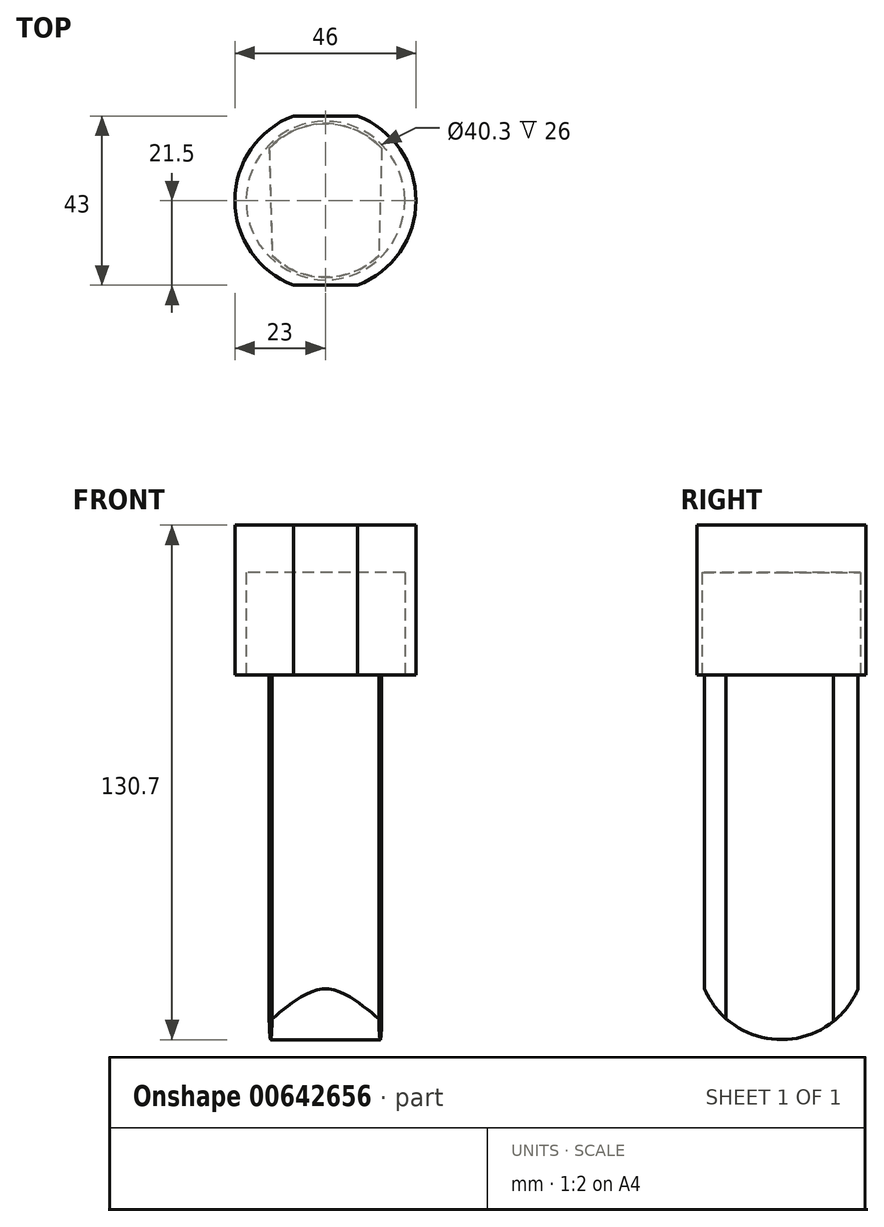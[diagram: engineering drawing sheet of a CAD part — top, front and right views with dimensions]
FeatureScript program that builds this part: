
annotation { "Feature Type Name" : "Feature", "Feature Type Description" : "" }
export const myFeature = defineFeature(function(context is Context, id is Id, definition is map)
    precondition{}
    {
        {
            var Q0;
            Q0=qCreatedBy(makeId("Top.planeOp"),FACE);
            var sketch = newSketch(context, id + "F0", { "sketchPlane" : qUnion([Q0])});
            skArc(sketch, "E0", {"start": v(-8.17, 21.5) * mm, "mid": v(-23, 0) * mm, "end": v(-8.17, -21.5) * mm});
            skLineSegment(sketch, "E1", {"start": v(-8.17, 21.5) * mm, "end": v(8.17, 21.5) * mm});
            skLineSegment(sketch, "E2.MirrorCS", {"start": v(-8.17, -21.5) * mm, "end": v(8.17, -21.5) * mm});
            skArc(sketch, "E3.trimOffspring", {"start": v(8.17, -21.5) * mm, "mid": v(23, 0) * mm, "end": v(8.17, 21.5) * mm});
            skSolve(sketch);
        }
        {
            var Q0;
            Q0 = qSketchRegion(id + "F0", true);
            var Q1;
            Q1=makeQuery(id+"F0.imprint","IMPRINT",FACE,{"disambiguationData":[TD([[makeQuery(id+"F0.imprint","IMPRINT",EDGE,{"derivedFrom":sQuery(id+"F0.wireOp",EDGE,"E0")}),1.0]])]});
            extrude(context, id + "F1", {"entities" : qUnion([Q0, Q1]), "depth" : 38 * mm, "offsetDistance" : 25.4 * mm});
        }
        {
            var Q0;
            Q0=qCreatedBy(makeId("Top.planeOp"),FACE);
            var sketch = newSketch(context, id + "F2", { "sketchPlane" : qUnion([Q0])});
            skCircle(sketch, "E4", {"center": v(0, 0) * mm, "radius": 20.15 * mm});
            skSolve(sketch);
        }
        {
            var Q0;
            Q0=makeQuery(id+"F2.imprint","IMPRINT",FACE,{"disambiguationData":[TD([[makeQuery(id+"F2.imprint","IMPRINT",EDGE,{"derivedFrom":sQuery(id+"F2.wireOp",EDGE,"E4")}),1.0]])]});
            extrude(context, id + "F3", {"entities" : qUnion([Q0]), "operationType" : NewBodyOperationType.REMOVE, "depth" : 26 * mm, "offsetDistance" : 25.4 * mm});
        }
        {
            var Q0;
            Q0=qCreatedBy(makeId("Top.planeOp"),FACE);
            var sketch = newSketch(context, id + "F4", { "sketchPlane" : qUnion([Q0])});
            skArc(sketch, "E5", {"start": v(-13.55, -14.02) * mm, "mid": v(0, -19.5) * mm, "end": v(13.55, -14.02) * mm});
            skLineSegment(sketch, "E6", {"start": v(-14.28, 13.28) * mm, "end": v(-13.55, -14.02) * mm});
            skLineSegment(sketch, "E7.MirrorCS", {"start": v(14.28, 13.28) * mm, "end": v(13.55, -14.02) * mm});
            skArc(sketch, "E8.trimOffspring", {"start": v(14.28, 13.28) * mm, "mid": v(0, 19.5) * mm, "end": v(-14.28, 13.28) * mm});
            skSolve(sketch);
        }
        {
            var Q0;
            Q0 = qSketchRegion(id + "F4", true);
            extrude(context, id + "F5", {"entities" : qUnion([Q0]), "oppositeDirection" : true, "depth" : 93 * mm, "offsetDistance" : 25.4 * mm});
        }
        {
            var Q0;
            Q0=qCreatedBy(makeId("Right.planeOp"),FACE);
            var sketch = newSketch(context, id + "F6", { "sketchPlane" : qUnion([Q0])});
            skCircle(sketch, "E9", {"center": v(0, -71.5) * mm, "radius": 21.2 * mm});
            skLineSegment(sketch, "E10", {"start": v(-20.95, -74.75) * mm, "end": v(-32.27, -102.2) * mm});
            skLineSegment(sketch, "E11", {"start": v(-32.27, -102.2) * mm, "end": v(31.4, -102.2) * mm});
            skLineSegment(sketch, "E12", {"start": v(31.4, -102.2) * mm, "end": v(19.84, -78.97) * mm});
            skSolve(sketch);
        }
        {
            var Q0;
            {var subQ0=sQuery(id+"F6.wireOp",EDGE,"E10");Q0=makeQuery(id+"F6.imprint","IMPRINT",FACE,{"disambiguationData":[TD([[makeQuery(id+"F6.imprint","IMPRINT",EDGE,{"derivedFrom":subQ0}),1.0]])]});}
            extrude(context, id + "F7", {"entities" : qUnion([Q0]), "operationType" : NewBodyOperationType.REMOVE, "endBound" : BoundingType.THROUGH_ALL, "depth" : 25.4 * mm, "offsetDistance" : 25.4 * mm});
        }
        {
            var Q0;
            Q0=makeQuery(id+"F7.boolean.opBoolean","COPY",FACE,{"derivedFrom":makeQuery(id+"F7.opExtrude","CAP_FACE",FACE,{"disambiguationData":[OSD([sQuery(id+"F6.wireOp",EDGE,"E9"),sQuery(id+"F6.wireOp",EDGE,"E10"),sQuery(id+"F6.wireOp",EDGE,"E11"),sQuery(id+"F6.wireOp",EDGE,"E12")])],"isStart":true})});
            extrude(context, id + "F8", {"entities" : qUnion([Q0]), "operationType" : NewBodyOperationType.REMOVE, "endBound" : BoundingType.THROUGH_ALL, "oppositeDirection" : true, "depth" : 25.4 * mm, "offsetDistance" : 25.4 * mm});
        }
    });
